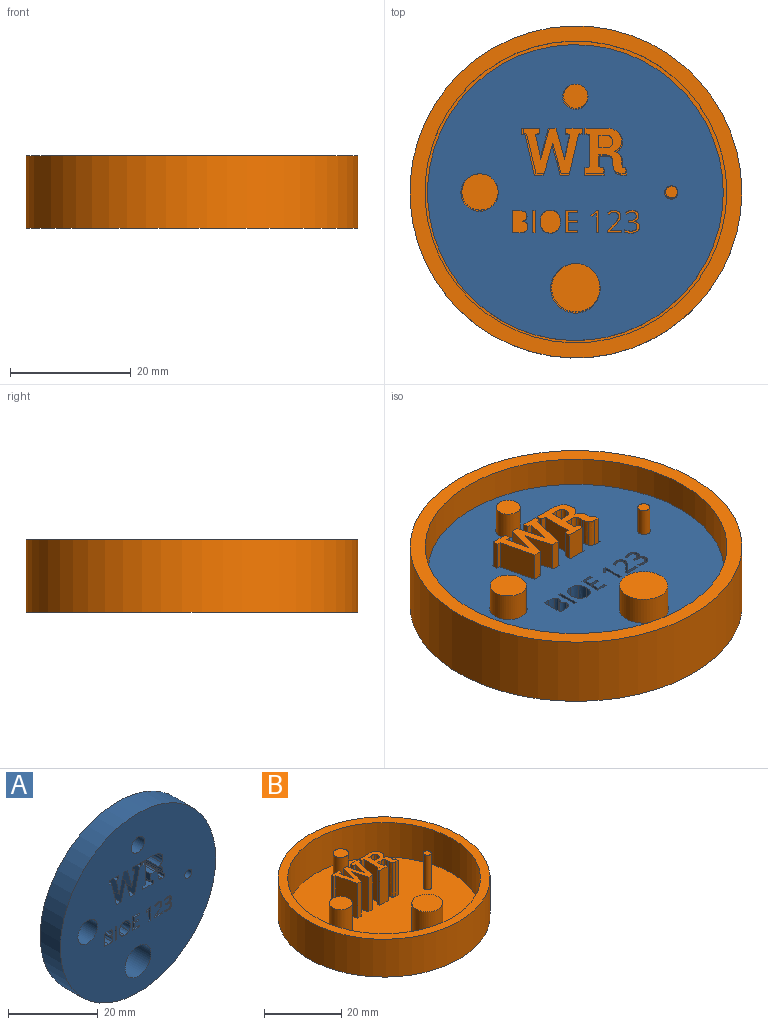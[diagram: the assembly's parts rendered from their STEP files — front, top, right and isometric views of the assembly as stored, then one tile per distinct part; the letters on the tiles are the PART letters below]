
ASSEMBLY  parts=2 mates=1
PART A: 151 faces, bbox 49x6.4x49 mm
  f0: plane 6.35x2.82mm, normal (0,0,-1), area 17.9mm2, adj f1,f135,f149,f150
  f1: plane 6.35x0.93mm, normal (-1,0,0), area 5.9mm2, adj f0,f2,f149,f150
  f2: plane 6.35x0.63mm, normal (-0.12,0,0.99), area 4.1mm2, adj f1,f3,f149,f150
  f3: plane 6.68x6.35mm, normal (-0.97,0,0.23), area 43.5mm2, adj f2,f4,f149,f150
  f4: plane 6.35x1.43mm, normal (0,0,1), area 9.1mm2, adj f3,f5,f149,f150
  f5: plane 6.35x5.07mm, normal (0.96,0,0.27), area 33.4mm2, adj f4,f6,f149,f150
  f6: plane 6.35x0.03mm, normal (0,0,1), area 0.2mm2, adj f5,f7,f149,f150
  f7: plane 6.35x5.07mm, normal (-0.96,0,0.27), area 33.4mm2, adj f6,f8,f149,f150
  f8: plane 6.35x1.43mm, normal (0,0,1), area 9.1mm2, adj f7,f9,f149,f150
  f9: plane 6.68x6.35mm, normal (0.97,0,0.23), area 43.5mm2, adj f8,f10,f149,f150
  f10: plane 6.35x0.63mm, normal (0.13,0,0.99), area 4mm2, adj f9,f11,f149,f150
  f11: plane 6.35x0.93mm, normal (1,0,0), area 5.9mm2, adj f10,f12,f149,f150
  f12: plane 6.35x2.83mm, normal (0,0,-1), area 18mm2, adj f11,f13,f149,f150
  f13: plane 6.35x0.93mm, normal (-1,0,0), area 5.9mm2, adj f12,f14,f149,f150
  f14: plane 6.35x0.7mm, normal (-0.17,0,0.99), area 4.5mm2, adj f13,f15,f149,f150
  f15: plane 6.35x4.21mm, normal (-0.98,0,-0.2), area 27.3mm2, adj f14,f16,f149,f150
  f16: plane 6.35x0.03mm, normal (-0.16,0,-0.99), area 0.2mm2, adj f15,f17,f149,f150
  f17: plane 6.35x5.27mm, normal (0.96,0,-0.26), area 34.7mm2, adj f16,f18,f149,f150
  f18: plane 6.35x1.13mm, normal (0,0,-1), area 7.2mm2, adj f17,f19,f149,f150
  f19: plane 6.35x5.27mm, normal (-0.96,0,-0.27), area 34.7mm2, adj f18,f20,f149,f150
  f20: plane 6.35x0.03mm, normal (0.16,0,-0.99), area 0.2mm2, adj f19,f21,f149,f150
  f21: plane 6.35x4.21mm, normal (0.98,0,-0.2), area 27.3mm2, adj f20,f22,f149,f150
  f22: plane 6.35x0.7mm, normal (0.17,0,0.99), area 4.5mm2, adj f21,f135,f149,f150
  f23: plane 6.35x3.45mm, normal (0,0,-1), area 21.9mm2, adj f24,f136,f149,f150
  f24: extruded ~6.35x2.05mm, area 13.8mm2, adj f23,f25,f149,f150
  f25: extruded ~6.35x1.65mm, area 11.9mm2, adj f24,f26,f149,f150
  f26: extruded ~6.35x1.01mm, area 6.8mm2, adj f25,f27,f149,f150
  f27: extruded ~6.35x0.91mm, area 7.4mm2, adj f26,f28,f149,f150
  f28: extruded ~6.35x0.98mm, area 7.7mm2, adj f27,f29,f149,f150
  f29: extruded ~6.35x1.16mm, area 7.7mm2, adj f28,f30,f149,f150
  f30: plane 6.35x0.39mm, normal (-1,0,0), area 2.5mm2, adj f29,f31,f149,f150
  f31: extruded ~6.35x0.39mm, area 2.6mm2, adj f30,f32,f149,f150
  f32: extruded ~6.35x0.33mm, area 2.4mm2, adj f31,f33,f149,f150
  f33: plane 6.35x0.19mm, normal (-0.14,0,-0.99), area 1.2mm2, adj f32,f34,f149,f150
  f34: plane 6.35x0.93mm, normal (-1,0,0), area 5.9mm2, adj f33,f35,f149,f150
  f35: plane 6.35x0.8mm, normal (0,0,1), area 5.1mm2, adj f34,f36,f149,f150
  f36: extruded ~6.35x1.06mm, area 7.5mm2, adj f35,f37,f149,f150
  f37: extruded ~6.35x1.05mm, area 7.1mm2, adj f36,f38,f149,f150
  f38: plane 6.35x0.44mm, normal (1,0,0), area 2.8mm2, adj f37,f39,f149,f150
  f39: extruded ~6.35x0.88mm, area 6mm2, adj f38,f40,f149,f150
  f40: extruded ~6.35x0.84mm, area 5.9mm2, adj f39,f41,f149,f150
  f41: plane 6.35x1.26mm, normal (0,0,1), area 8mm2, adj f40,f42,f149,f150
  f42: plane 6.35x2.03mm, normal (-1,0,0), area 12.9mm2, adj f41,f43,f149,f150
  f43: plane 6.35x0.82mm, normal (-0.19,0,-0.98), area 5.3mm2, adj f42,f44,f149,f150
  f44: plane 6.35x0.92mm, normal (-1,0,0), area 5.9mm2, adj f43,f45,f149,f150
  f45: plane 6.35x3.18mm, normal (0,0,1), area 20.2mm2, adj f44,f46,f149,f150
  f46: plane 6.35x0.92mm, normal (1,0,0), area 5.9mm2, adj f45,f47,f149,f150
  f47: plane 6.35x0.82mm, normal (0.19,0,-0.98), area 5.3mm2, adj f46,f48,f149,f150
  f48: plane 6.35x5.51mm, normal (1,0,0), area 35mm2, adj f47,f49,f149,f150
  f49: plane 6.35x0.82mm, normal (0.19,0,0.98), area 5.3mm2, adj f48,f136,f149,f150
  f50: plane 6.35x1.29mm, normal (0,0,1), area 8.2mm2, adj f51,f137,f149,f150
  f51: plane 6.35x3.69mm, normal (1,0,0), area 23.4mm2, adj f50,f52,f149,f150
  f52: plane 6.35x1.04mm, normal (0,0,-1), area 6.6mm2, adj f51,f53,f149,f150
  f53: extruded ~6.35x1.06mm, area 7mm2, adj f52,f54,f149,f150
  f54: extruded ~6.35x0.69mm, area 5.1mm2, adj f53,f55,f149,f150
  f55: extruded ~6.35x0.54mm, area 3.7mm2, adj f54,f56,f149,f150
  f56: extruded ~6.35x0.53mm, area 3.9mm2, adj f55,f57,f149,f150
  f57: plane 6.35x0.03mm, normal (-1,0,0), area 0.2mm2, adj f56,f58,f149,f150
  f58: extruded ~6.35x0.88mm, area 8.6mm2, adj f57,f59,f149,f150
  f59: extruded ~6.35x0.77mm, area 5.5mm2, adj f58,f137,f149,f150
  f60: plane 6.35x3.69mm, normal (-1,0,0), area 23.4mm2, adj f61,f138,f149,f150
  f61: plane 6.35x0.43mm, normal (0,0,1), area 2.7mm2, adj f60,f62,f149,f150
  f62: plane 6.35x3.69mm, normal (1,0,0), area 23.4mm2, adj f61,f138,f149,f150
  f63: extruded ~6.35x1.24mm, area 8.8mm2, adj f64,f139,f149,f150
  f64: extruded ~6.35x1.39mm, area 9.5mm2, adj f63,f65,f149,f150
  f65: extruded ~6.35x1.39mm, area 9.5mm2, adj f64,f66,f149,f150
  f66: extruded ~6.35x1.24mm, area 8.8mm2, adj f65,f67,f149,f150
  f67: extruded ~6.35x1.26mm, area 8.9mm2, adj f66,f68,f149,f150
  f68: extruded ~6.35x1.41mm, area 9.6mm2, adj f67,f69,f149,f150
  f69: extruded ~6.35x1.4mm, area 9.5mm2, adj f68,f139,f149,f150
  f70: plane 6.35x1.63mm, normal (0,0,-1), area 10.3mm2, adj f71,f140,f149,f150
  f71: plane 6.35x0.38mm, normal (-1,0,0), area 2.4mm2, adj f70,f72,f149,f150
  f72: plane 6.35x2.05mm, normal (0,0,1), area 13mm2, adj f71,f73,f149,f150
  f73: plane 6.35x3.69mm, normal (1,0,0), area 23.4mm2, adj f72,f74,f149,f150
  f74: plane 6.35x2.05mm, normal (0,0,-1), area 13mm2, adj f73,f75,f149,f150
  f75: plane 6.35x0.38mm, normal (-1,0,0), area 2.4mm2, adj f74,f76,f149,f150
  f76: plane 6.35x1.63mm, normal (0,0,1), area 10.3mm2, adj f75,f77,f149,f150
  f77: plane 6.35x1.19mm, normal (-1,0,0), area 7.5mm2, adj f76,f78,f149,f150
  f78: plane 6.35x1.53mm, normal (0,0,-1), area 9.7mm2, adj f77,f79,f149,f150
  f79: plane 6.35x0.38mm, normal (-1,0,0), area 2.4mm2, adj f78,f80,f149,f150
  f80: plane 6.35x1.53mm, normal (0,0,1), area 9.7mm2, adj f79,f140,f149,f150
  f81: plane 6.35x0.35mm, normal (0,0,-1), area 2.2mm2, adj f82,f141,f149,f150
  f82: plane 6.35x3.69mm, normal (-1,0,0), area 23.4mm2, adj f81,f83,f149,f150
  f83: plane 6.35x0.41mm, normal (0,0,1), area 2.6mm2, adj f82,f84,f149,f150
  f84: plane 6.35x2.63mm, normal (1,0,0), area 16.7mm2, adj f83,f85,f149,f150
  f85: extruded ~6.35x0.62mm, area 3.9mm2, adj f84,f86,f149,f150
  f86: extruded ~6.35x0.12mm, area 1mm2, adj f85,f87,f149,f150
  f87: extruded ~6.35x0.6mm, area 4.9mm2, adj f86,f88,f149,f150
  f88: plane 6.35x0.29mm, normal (0.79,0,0.61), area 2.3mm2, adj f87,f141,f149,f150
  f89: plane 6.35x1.9mm, normal (0,0,-1), area 12mm2, adj f90,f142,f149,f150
  f90: plane 6.35x0.39mm, normal (-1,0,0), area 2.5mm2, adj f89,f91,f149,f150
  f91: plane 6.35x2.42mm, normal (0,0,1), area 15.4mm2, adj f90,f92,f149,f150
  f92: plane 6.35x0.36mm, normal (1,0,0), area 2.3mm2, adj f91,f93,f149,f150
  f93: plane 6.35x0.98mm, normal (0.71,0,-0.71), area 8.7mm2, adj f92,f94,f149,f150
  f94: extruded ~6.35x0.64mm, area 5.5mm2, adj f93,f95,f149,f150
  f95: extruded ~6.35x0.37mm, area 2.7mm2, adj f94,f96,f149,f150
  f96: extruded ~6.35x0.39mm, area 2.5mm2, adj f95,f97,f149,f150
  f97: extruded ~6.35x0.47mm, area 3.3mm2, adj f96,f98,f149,f150
  f98: extruded ~6.35x0.5mm, area 3.4mm2, adj f97,f99,f149,f150
  f99: extruded ~6.35x0.44mm, area 2.8mm2, adj f98,f100,f149,f150
  f100: extruded ~6.35x0.46mm, area 3.4mm2, adj f99,f101,f149,f150
  f101: plane 6.35x0.28mm, normal (0.79,0,0.61), area 2.3mm2, adj f100,f102,f149,f150
  f102: extruded ~6.35x1.11mm, area 7.7mm2, adj f101,f103,f149,f150
  f103: extruded ~6.35x0.81mm, area 5.6mm2, adj f102,f104,f149,f150
  f104: extruded ~6.35x0.71mm, area 5.1mm2, adj f103,f105,f149,f150
  f105: extruded ~6.35x0.69mm, area 4.6mm2, adj f104,f106,f149,f150
  f106: extruded ~6.35x0.87mm, area 7.2mm2, adj f105,f107,f149,f150
  f107: plane 6.35x0.81mm, normal (-0.7,0,0.71), area 7.2mm2, adj f106,f142,f149,f150
  f108: extruded ~6.35x0.83mm, area 5.6mm2, adj f109,f143,f149,f150
  f109: extruded ~6.35x0.67mm, area 4.8mm2, adj f108,f110,f149,f150
  f110: extruded ~6.35x0.58mm, area 4mm2, adj f109,f111,f149,f150
  f111: extruded ~6.35x0.56mm, area 4.1mm2, adj f110,f112,f149,f150
  f112: plane 6.35x0.02mm, normal (-1,0,0), area 0.1mm2, adj f111,f113,f149,f150
  f113: extruded ~6.35x0.66mm, area 4.6mm2, adj f112,f114,f149,f150
  f114: extruded ~6.35x0.6mm, area 4.1mm2, adj f113,f115,f149,f150
  f115: extruded ~6.35x0.81mm, area 5.9mm2, adj f114,f116,f149,f150
  f116: extruded ~6.35x1.04mm, area 7mm2, adj f115,f117,f149,f150
  f117: extruded ~6.35x0.54mm, area 3.4mm2, adj f116,f118,f149,f150
  f118: extruded ~6.35x0.47mm, area 3.2mm2, adj f117,f119,f149,f150
  f119: plane 6.35x0.4mm, normal (1,0,0), area 2.5mm2, adj f118,f120,f149,f150
  f120: extruded ~6.35x0.51mm, area 3.4mm2, adj f119,f121,f149,f150
  f121: extruded ~6.35x0.51mm, area 3.3mm2, adj f120,f122,f149,f150
  f122: extruded ~6.35x0.96mm, area 8.8mm2, adj f121,f123,f149,f150
  f123: extruded ~6.35x1.05mm, area 9mm2, adj f122,f124,f149,f150
  f124: plane 6.35x0.36mm, normal (0,0,1), area 2.3mm2, adj f123,f125,f149,f150
  f125: plane 6.35x0.36mm, normal (1,0,0), area 2.3mm2, adj f124,f126,f149,f150
  f126: plane 6.35x0.37mm, normal (0,0,-1), area 2.3mm2, adj f125,f127,f149,f150
  f127: extruded ~6.35x0.68mm, area 4.6mm2, adj f126,f128,f149,f150
  f128: extruded ~6.35x0.53mm, area 3.9mm2, adj f127,f129,f149,f150
  f129: extruded ~6.35x0.42mm, area 3mm2, adj f128,f130,f149,f150
  f130: extruded ~6.35x0.5mm, area 3.4mm2, adj f129,f131,f149,f150
  f131: extruded ~6.35x0.46mm, area 2.9mm2, adj f130,f132,f149,f150
  f132: extruded ~6.35x0.49mm, area 3.5mm2, adj f131,f133,f149,f150
  f133: plane 6.35x0.28mm, normal (0.8,0,0.6), area 2.2mm2, adj f132,f134,f149,f150
  f134: extruded ~6.35x0.52mm, area 3.8mm2, adj f133,f143,f149,f150
  f135: plane 6.35x0.93mm, normal (1,0,0), area 5.9mm2, adj f0,f22,f149,f150
  f136: plane 6.35x0.93mm, normal (1,0,0), area 5.9mm2, adj f23,f49,f149,f150
  f137: extruded ~6.35x0.93mm, area 6.3mm2, adj f50,f59,f149,f150
  f138: plane 6.35x0.43mm, normal (0,0,-1), area 2.7mm2, adj f60,f62,f149,f150
  f139: extruded ~6.35x1.26mm, area 8.9mm2, adj f63,f69,f149,f150
  f140: plane 6.35x1.36mm, normal (-1,0,0), area 8.6mm2, adj f70,f80,f149,f150
  f141: plane 6.35x0.98mm, normal (0.61,0,-0.79), area 7.8mm2, adj f81,f88,f149,f150
  f142: plane 6.35x0.02mm, normal (-1,0,0), area 0.1mm2, adj f89,f107,f149,f150
  f143: extruded ~6.35x0.62mm, area 4mm2, adj f108,f134,f149,f150
  f144: cylinder r=3.1mm len=6.35mm, axis (0,1,0), area 123.7mm2, adj f149,f150
  f145: cylinder r=2.1mm len=6.35mm, axis (0,1,0), area 83.8mm2, adj f149,f150
  f146: cylinder r=1.1mm len=6.35mm, axis (0,1,0), area 43.9mm2, adj f149,f150
  f147: cylinder r=4.1mm len=8.2mm, axis (0,1,0), area 163.6mm2, adj f149,f150
  f148: cylinder r=24.5mm len=49mm, axis (0,1,0), area 977.5mm2, adj f149,f150
  f149: plane 49x49mm, normal (0,-1,0), area 1678.6mm2, adj f0,f1,f2,f3,f4,f5,f6,f7
  f150: plane 49x49mm, normal (0,1,0), area 1678.6mm2, adj f0,f1,f2,f3,f4,f5,f6,f7
PART B: 75 faces, bbox 55x55x12 mm
  f0: plane 50x50mm, normal (0,0,1), area 1798.8mm2, adj f1,f5,f6,f7,f8,f9,f10,f11
  f1: cylinder r=25mm len=50mm, axis (0,0,-1), area 1727.9mm2, adj f0,f3
  f2: cylinder r=27.5mm len=55mm, axis (0,0,-1), area 2073.5mm2, adj f3,f4
  f3: plane 55x55mm, normal (0,0,1), area 412.3mm2, adj f1,f2
  f4: plane 55x55mm, normal (0,0,-1), area 2375.8mm2, adj f2
  f5: plane 11x0.9mm, normal (1,0,0), area 9.9mm2, adj f0,f6,f28,f29
  f6: plane 11x2.75mm, normal (0,1,0), area 30.2mm2, adj f0,f5,f7,f29
  f7: plane 11x0.9mm, normal (-1,0,0), area 9.9mm2, adj f0,f6,f8,f29
  f8: plane 11x0.68mm, normal (-0.17,-0.99,0), area 7.6mm2, adj f0,f7,f9,f29
  f9: plane 11x4.09mm, normal (-0.98,0.2,0), area 46mm2, adj f0,f8,f10,f29
  f10: plane 11x0.03mm, normal (-0.16,0.99,0), area 0.3mm2, adj f0,f9,f11,f29
  f11: plane 11x5.12mm, normal (0.96,0.27,0), area 58.4mm2, adj f0,f10,f12,f29
  f12: plane 11x1.1mm, normal (0,1,0), area 12.1mm2, adj f0,f11,f13,f29
  f13: plane 11x5.12mm, normal (-0.96,0.26,0), area 58.4mm2, adj f0,f12,f14,f29
  f14: plane 11x0.03mm, normal (0.16,0.99,0), area 0.3mm2, adj f0,f13,f15,f29
  f15: plane 11x4.09mm, normal (0.98,0.2,0), area 46mm2, adj f0,f14,f16,f29
  f16: plane 11x0.68mm, normal (0.17,-0.99,0), area 7.6mm2, adj f0,f15,f17,f29
  f17: plane 11x0.9mm, normal (1,0,0), area 9.9mm2, adj f0,f16,f18,f29
  f18: plane 11x2.75mm, normal (0,1,0), area 30.2mm2, adj f0,f17,f19,f29
  f19: plane 11x0.9mm, normal (-1,0,0), area 9.9mm2, adj f0,f18,f20,f29
  f20: plane 11x0.61mm, normal (-0.13,-0.99,0), area 6.8mm2, adj f0,f19,f21,f29
  f21: plane 11x6.49mm, normal (-0.97,-0.23,0), area 73.3mm2, adj f0,f20,f22,f29
  f22: plane 11x1.39mm, normal (0,-1,0), area 15.3mm2, adj f0,f21,f23,f29
  f23: plane 11x4.93mm, normal (0.96,-0.27,0), area 56.3mm2, adj f0,f22,f24,f29
  f24: plane 11x0.03mm, normal (0,-1,0), area 0.3mm2, adj f0,f23,f25,f29
  f25: plane 11x4.93mm, normal (-0.96,-0.27,0), area 56.3mm2, adj f0,f24,f26,f29
  f26: plane 11x1.39mm, normal (0,-1,0), area 15.3mm2, adj f0,f25,f27,f29
  f27: plane 11x6.49mm, normal (0.97,-0.23,0), area 73.3mm2, adj f0,f26,f28,f29
  f28: plane 11x0.62mm, normal (0.12,-0.99,0), area 6.8mm2, adj f0,f5,f27,f29
  f29: plane 9.81x7.47mm, normal (0,0,1), area 37.1mm2, adj f5,f6,f7,f8,f9,f10,f11,f12
  f30: plane 11x3.36mm, normal (0,1,0), area 36.9mm2, adj f0,f31,f64,f65
  f31: plane 11x0.9mm, normal (-1,0,0), area 9.9mm2, adj f0,f30,f32,f65
  f32: plane 11x0.79mm, normal (-0.19,-0.98,0), area 8.9mm2, adj f0,f31,f33,f65
  f33: plane 11x5.36mm, normal (-1,0,0), area 59mm2, adj f0,f32,f34,f65
  f34: plane 11x0.79mm, normal (-0.19,0.98,0), area 8.9mm2, adj f0,f33,f35,f65
  f35: plane 11x0.9mm, normal (-1,0,0), area 9.9mm2, adj f0,f34,f36,f65
  f36: plane 11x3.09mm, normal (0,-1,0), area 34mm2, adj f0,f35,f37,f65
  f37: plane 11x0.9mm, normal (1,0,0), area 9.9mm2, adj f0,f36,f38,f65
  f38: plane 11x0.8mm, normal (0.19,0.98,0), area 9mm2, adj f0,f37,f39,f65
  f39: plane 11x1.97mm, normal (1,0,0), area 21.7mm2, adj f0,f38,f40,f65
  f40: plane 11x1.23mm, normal (0,-1,0), area 13.5mm2, adj f0,f39,f41,f65
  f41: extruded ~11x0.82mm, area 10mm2, adj f0,f40,f42,f65
  f42: extruded ~11x0.85mm, area 10.2mm2, adj f0,f41,f43,f65
  f43: plane 11x0.43mm, normal (-1,0,0), area 4.7mm2, adj f0,f42,f44,f65
  f44: extruded ~11x1.02mm, area 11.9mm2, adj f0,f43,f45,f65
  f45: extruded ~11x1.03mm, area 12.6mm2, adj f0,f44,f46,f65
  f46: plane 11x0.78mm, normal (0,-1,0), area 8.5mm2, adj f0,f45,f47,f65
  f47: plane 11x0.9mm, normal (1,0,0), area 9.9mm2, adj f0,f46,f48,f65
  f48: plane 11x0.18mm, normal (0.14,0.99,0), area 2mm2, adj f0,f47,f49,f65
  f49: extruded ~11x0.32mm, area 4.1mm2, adj f0,f48,f50,f65
  f50: extruded ~11x0.38mm, area 4.4mm2, adj f0,f49,f51,f65
  f51: plane 11x0.38mm, normal (1,0,0), area 4.2mm2, adj f0,f50,f52,f65
  f52: extruded ~11x1.13mm, area 13mm2, adj f0,f51,f53,f65
  f53: extruded ~11x0.95mm, area 12.9mm2, adj f0,f52,f54,f65
  f54: extruded ~11x0.89mm, area 12.4mm2, adj f0,f53,f55,f65
  f55: extruded ~11x0.98mm, area 11.5mm2, adj f0,f54,f56,f65
  f56: extruded ~11x1.61mm, area 20.1mm2, adj f0,f55,f64,f65
  f57: plane 11x2.14mm, normal (1,0,0), area 23.5mm2, adj f58,f63,f65,f66
  f58: plane 11x1.06mm, normal (0,-1,0), area 11.7mm2, adj f57,f59,f65,f66
  f59: extruded ~11x0.92mm, area 10.9mm2, adj f58,f60,f65,f66
  f60: extruded ~11x0.8mm, area 9.7mm2, adj f59,f61,f65,f66
  f61: extruded ~11x0.77mm, area 9.4mm2, adj f60,f62,f65,f66
  f62: extruded ~11x0.94mm, area 11mm2, adj f61,f63,f65,f66
  f63: plane 11x1.04mm, normal (0,1,0), area 11.4mm2, adj f57,f62,f65,f66
  f64: extruded ~11x2mm, area 23.3mm2, adj f0,f30,f56,f65
  f65: plane 7.47x6.73mm, normal (0,0,1), area 28.9mm2, adj f30,f31,f32,f33,f34,f35,f36,f37
  f66: plane 2.29x2.14mm, normal (0,0,1), area 4.4mm2, adj f57,f58,f59,f60,f61,f62,f63
  f67: cylinder r=3mm len=11mm, axis (0,0,-1), area 207.3mm2, adj f0,f68
  f68: plane 6x6mm, normal (0,0,1), area 28.3mm2, adj f67
  f69: cylinder r=4mm len=11mm, axis (0,0,-1), area 276.5mm2, adj f0,f70
  f70: plane 8x8mm, normal (0,0,1), area 50.3mm2, adj f69
  f71: cylinder r=2mm len=11mm, axis (0,0,-1), area 138.2mm2, adj f0,f72
  f72: plane 4x4mm, normal (0,0,1), area 12.6mm2, adj f71
  f73: cylinder r=1mm len=11mm, axis (0,0,-1), area 69.1mm2, adj f0,f74
  f74: plane 2x2mm, normal (0,0,1), area 3.1mm2, adj f73
PLACE A rot(axis=(-1,0,0),90deg) t=(0,0,69.3)mm
PLACE B t=(0.07,0.1,68.3)mm
MATE fastened B.f0 <-> A.f150  axis (0,0,1) through (0.29,0.15,69.3)mm
